# Revit family: 2023673
name_source: partatom
category: Lighting Fixtures
revit_build: Autodesk Revit 2018 (Build: 20170223_1515(x64)
units: mm (PartAtom-declared; Revit-internal decimal feet)

## family parameters
Cut with Voids When Loaded = No
Host = Face
Light Source = No
OmniClass Number = 23.80.70.00
OmniClass Title = Lighting
Part Type = Normal
Room Calculation Point = No
Round Connector Dimension = Use Diameter
Shared = No

## types (1)
- 2023673 OPTIX R 1200 2L 4K C9 WHT
    Apparent Load = 25 VA
    Assembly Code = D5020200
    AssetType = Fixed
    ClassificationName = Uniclass2015
    ClassificationValue = EF_70_80
    Cost = 0 $
    Default Elevation = 1219 mm
    Description = OPTIX RECESSED 1200x300 2L 4000K C9 WHT is a high efficacy low glare luminaire for office and education applications with excellent colour rendering. Ceiling recessed 1200x300 mm. White plastic low glare optics in 2 lines configuration. White RAL9016 fixture body. Constant current driver. 4000K Neutral White LED, CRI>90, chromaticity tolerance of 3-step MacAdam ellipse. Luminous flux 3500lm. Power consumption 25W. Luminaire efficacy 140lm/W. Lifespan: 48,500 hours L90B10. UGR<19, Luminance at 65°<3000 Cd/m2, IK07, IP20. Photobiological safety risk group 0. Electrical protection Class I. Glow wire test 850°C.
    DocumentationLiterature = http://www.sylvania-lighting.com
    DurationUnit = hours
    ElectricShockClassification = 140
    ExpectedLife = 50000
    Height = 38 mm  [stored 0.124672 ft]
    IfcExportAs = Class I
    IfcExportType = IfcLightFixtureType
    ImpactProtectionIndex = IfcLightFixtureType
    IngressProtection = IfcLightFixtureType
    InputNominalFrequency = 4000
    InputVoltage = 0
    LampColourRenderingIndex = 16500
    LampColourTemperature = LED
    LampMacAdamStep = 90
    LampNominalLuminous = 4000 K
    Length = 1196 mm  [stored 3.92388 ft]
    LightOutputRatio = LED
    LuminaireType = 0
    ManufacturerName = 140 lm/W
    Material = Feilo Sylvania
    Material_1_FEILO = <By Category>
    Material_2_FEILO = <By Category>
    Material_3_FEILO = <By Category>
    Material_4_FEILO = <By Category>
    Model = OPTIX RECESSED 1200 2L 4000K C9 WHT
    ModelNumber = 2023673
    ModelReference = OPTIX RECESSED 1200 2L 4000K C9 WHT
    Name = OPTIX RECESSED 1200 2L 4000K C9 WHT
    NominalDepth = 296 mm  [stored 0.971129 ft]
    NominalHeight = 38 mm  [stored 0.124672 ft]
    NominalLength = 296 mm  [stored 0.971129 ft]
    PowerConsumption = Lighting
    PowerFactor = 0.95
    Type Image = <None>
    TypeName = OPTIX RECESSED 1200 2L 4000K C9 WHT
    URL = 0.95
    Voltage = 230 V
    WarrantyDescription = http://www.sylvania-lighting.com
    Width = 296 mm  [stored 0.971129 ft]

note: [stored X ft] marks values corroborated as IEEE doubles in the binary element streams (Revit-internal decimal feet)

## geometry (parser evidence)
native form markers: Sweep x4
no freeform markers — native parametric forms only
